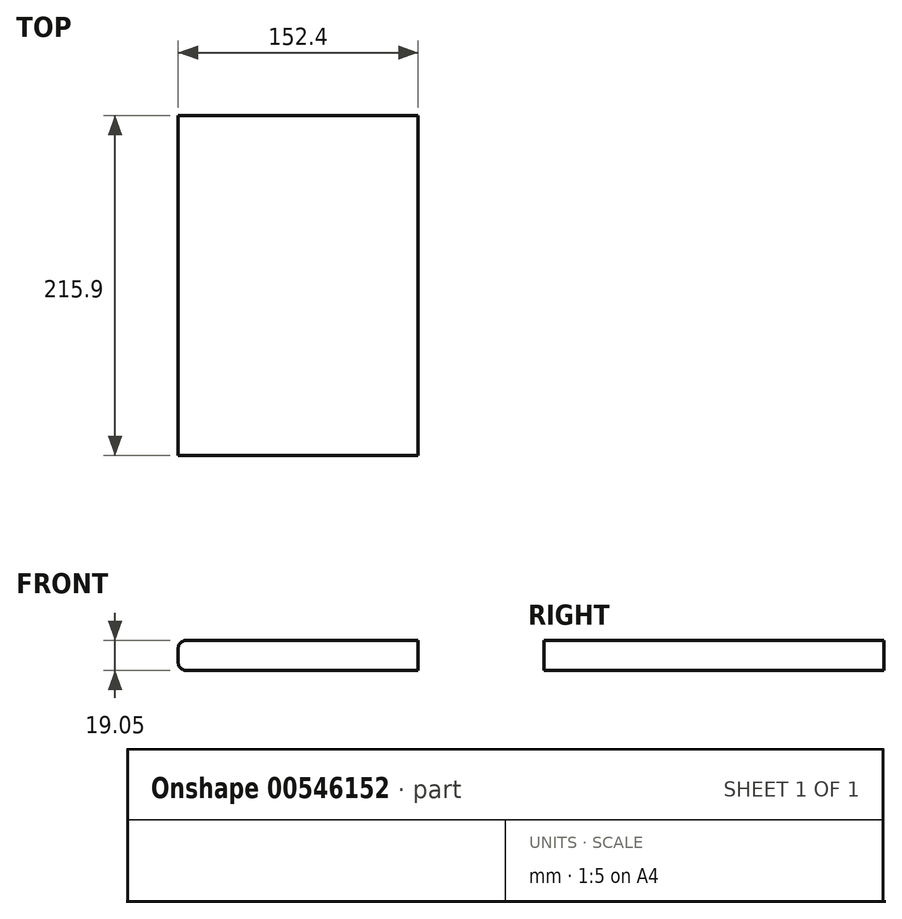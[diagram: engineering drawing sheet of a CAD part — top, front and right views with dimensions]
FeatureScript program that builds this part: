
annotation { "Feature Type Name" : "Feature", "Feature Type Description" : "" }
export const myFeature = defineFeature(function(context is Context, id is Id, definition is map)
    precondition{}
    {
        {
            var Q0;
            Q0=qCreatedBy(makeId("Top.planeOp"),FACE);
            var sketch = newSketch(context, id + "F0", { "sketchPlane" : qUnion([Q0])});
            skLineSegment(sketch, "E0.bottom", {"start": v(0, 0) * mm, "end": v(-152.4, 0) * mm});
            skLineSegment(sketch, "E0.top", {"start": v(0, -215.9) * mm, "end": v(-152.4, -215.9) * mm});
            skLineSegment(sketch, "E0.left", {"start": v(0, 0) * mm, "end": v(0, -215.9) * mm});
            skLineSegment(sketch, "E0.right", {"start": v(-152.4, 0) * mm, "end": v(-152.4, -215.9) * mm});
            skSolve(sketch);
        }
        {
            var Q0;
            Q0=makeQuery(id+"F0.imprint","IMPRINT",FACE,{"disambiguationData":[TD([[makeQuery(id+"F0.imprint","IMPRINT",EDGE,{"derivedFrom":sQuery(id+"F0.wireOp",EDGE,"E0.bottom")}),1.0]])]});
            extrude(context, id + "F1", {"entities" : qUnion([Q0]), "depth" : 19.05 * mm, "offsetDistance" : 25.4 * mm});
        }
        {
            var Q0;
            Q0=makeQuery(id+"F1.opExtrude","CAP_EDGE",EDGE,{"disambiguationData":[OSD([sQuery(id+"F0.wireOp",EDGE,"E0.right")])],"isStart":false});
            fillet(context, id + "F2", {"entities" : qUnion([Q0]), "radius" : 5.08 * mm, "tangentPropagation" : true, "allowEdgeOverflow" : false});
        }
        {
            var Q0;
            Q0=makeQuery(id+"F1.opExtrude","CAP_EDGE",EDGE,{"disambiguationData":[OSD([sQuery(id+"F0.wireOp",EDGE,"E0.right")])],"isStart":true});
            fillet(context, id + "F3", {"entities" : qUnion([Q0]), "radius" : 5.08 * mm, "tangentPropagation" : true, "allowEdgeOverflow" : false});
        }
    });
